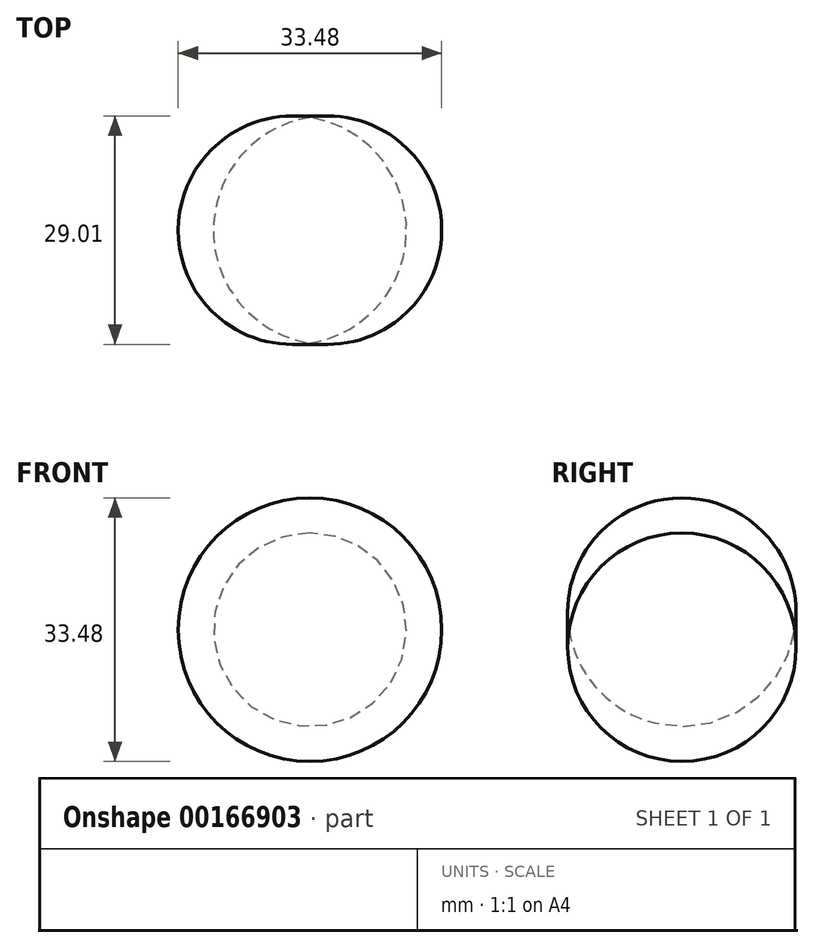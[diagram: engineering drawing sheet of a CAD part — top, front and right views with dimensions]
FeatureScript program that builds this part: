
annotation { "Feature Type Name" : "Feature", "Feature Type Description" : "" }
export const myFeature = defineFeature(function(context is Context, id is Id, definition is map)
    precondition{}
    {
        {
            var Q0;
            Q0=qCreatedBy(makeId("Top.planeOp"),FACE);
            var sketch = newSketch(context, id + "F0", { "sketchPlane" : qUnion([Q0])});
            skArc(sketch, "E0", {"start": v(0, 28.67) * mm, "mid": v(-12.28, 14.34) * mm, "end": v(0, 0) * mm});
            skLineSegment(sketch, "E1", {"start": v(0, 0) * mm, "end": v(0, 28.67) * mm});
            skSolve(sketch);
        }
        {
            var Q0;
            Q0=makeQuery(id+"F0.imprint","IMPRINT",FACE,{"disambiguationData":[TD([[makeQuery(id+"F0.imprint","IMPRINT",EDGE,{"derivedFrom":sQuery(id+"F0.wireOp",EDGE,"E0")}),1.0]])]});
            var Q1;
            Q1=sQuery(id+"F0.wireOp",EDGE,"E1");
            revolve(context, id + "F1", {"entities" : qUnion([Q0]), "axis" : qUnion([Q1]), "revolveType" : RevolveType.FULL});
        }
    });
